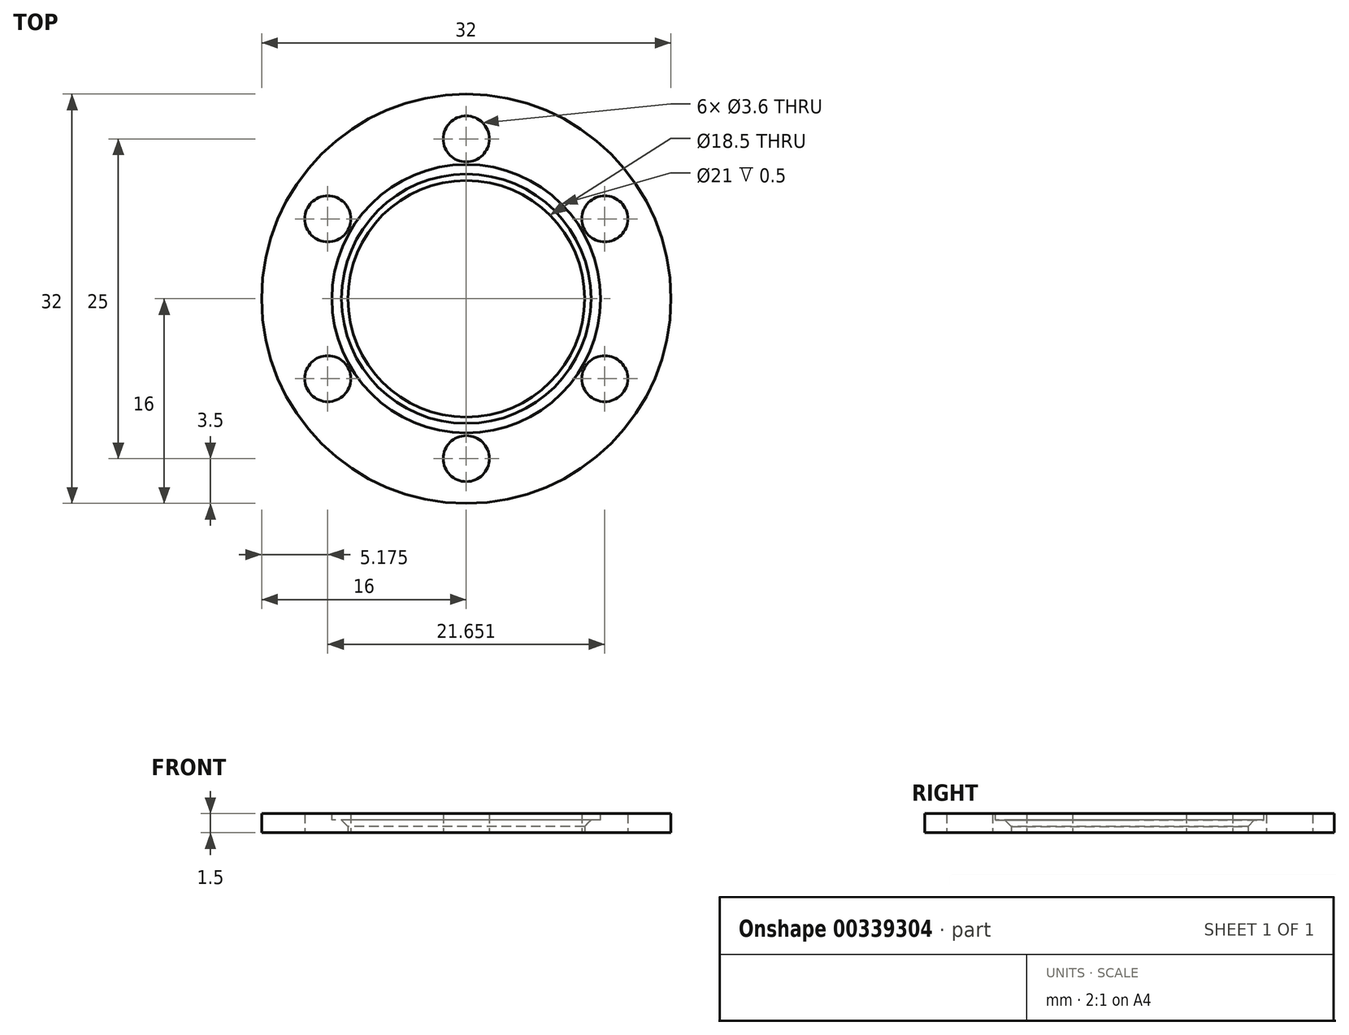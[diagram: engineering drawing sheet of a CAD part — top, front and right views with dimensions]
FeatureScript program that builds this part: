
annotation { "Feature Type Name" : "Feature", "Feature Type Description" : "" }
export const myFeature = defineFeature(function(context is Context, id is Id, definition is map)
    precondition{}
    {
        {
            var Q0;
            Q0=qCreatedBy(makeId("Top.planeOp"),FACE);
            var sketch = newSketch(context, id + "F0", { "sketchPlane" : qUnion([Q0])});
            skCircle(sketch, "E0", {"center": v(0, 0) * mm, "radius": 16 * mm});
            skCircle(sketch, "E1", {"center": v(0, 0) * mm, "radius": 2 * mm, "construction": true});
            skCircle(sketch, "E2", {"center": v(0, 0) * mm, "radius": 12.5 * mm, "construction": true});
            skCircle(sketch, "E3", {"center": v(0, 0) * mm, "radius": 10.5 * mm, "construction": true});
            skCircle(sketch, "E4", {"center": v(0, 12.5) * mm, "radius": 1.8 * mm});
            skCircle(sketch, "E5.1.0", {"center": v(-10.83, 6.25) * mm, "radius": 1.8 * mm});
            skCircle(sketch, "E5.2.0", {"center": v(-10.83, -6.25) * mm, "radius": 1.8 * mm});
            skCircle(sketch, "E5.3.0", {"center": v(0, -12.5) * mm, "radius": 1.8 * mm});
            skCircle(sketch, "E5.4.0", {"center": v(10.83, -6.25) * mm, "radius": 1.8 * mm});
            skCircle(sketch, "E5.5.0", {"center": v(10.83, 6.25) * mm, "radius": 1.8 * mm});
            skCircle(sketch, "E6", {"center": v(0, 0) * mm, "radius": 9.25 * mm});
            skSolve(sketch);
        }
        {
            var Q0;
            Q0 = qSketchRegion(id + "F0", true);
            extrude(context, id + "F1", {"entities" : qUnion([Q0]), "depth" : 1.5 * mm, "offsetDistance" : 25 * mm});
        }
        {
            var Q0;
            Q0=makeQuery(id+"F1.opExtrude","CAP_FACE",FACE,{"disambiguationData":[OSD([sQuery(id+"F0.wireOp",EDGE,"E0"),sQuery(id+"F0.wireOp",EDGE,"E4"),sQuery(id+"F0.wireOp",EDGE,"E5.1.0"),sQuery(id+"F0.wireOp",EDGE,"E5.2.0"),sQuery(id+"F0.wireOp",EDGE,"E5.3.0"),sQuery(id+"F0.wireOp",EDGE,"E5.4.0"),sQuery(id+"F0.wireOp",EDGE,"E5.5.0"),sQuery(id+"F0.wireOp",EDGE,"E6")])],"isStart":false});
            var sketch = newSketch(context, id + "F2", { "sketchPlane" : qUnion([Q0])});
            skCircle(sketch, "E7", {"center": v(0, 0) * mm, "radius": 10.5 * mm});
            skSolve(sketch);
        }
        {
            var Q0;
            Q0 = qSketchRegion(id + "F2", true);
            extrude(context, id + "F3", {"entities" : qUnion([Q0]), "operationType" : NewBodyOperationType.REMOVE, "oppositeDirection" : true, "depth" : 0.5 * mm, "offsetDistance" : 25 * mm});
        }
        {
            var Q0;
            Q0=makeQuery(id+"F3.boolean.opBoolean","INTERSECT",EDGE,{"derivedFrom":[makeQuery(id+"F1.opExtrude","SWEPT_FACE",FACE,{"disambiguationData":[OSD([sQuery(id+"F0.wireOp",EDGE,"E6")])]}),makeQuery(id+"F3.opExtrude","CAP_FACE",FACE,{"disambiguationData":[OSD([sQuery(id+"F2.wireOp",EDGE,"E7")])],"isStart":false})]});
            chamfer(context, id + "F4", {"entities" : qUnion([Q0]), "width" : 0.5 * mm, "tangentPropagation" : true});
        }
    });
